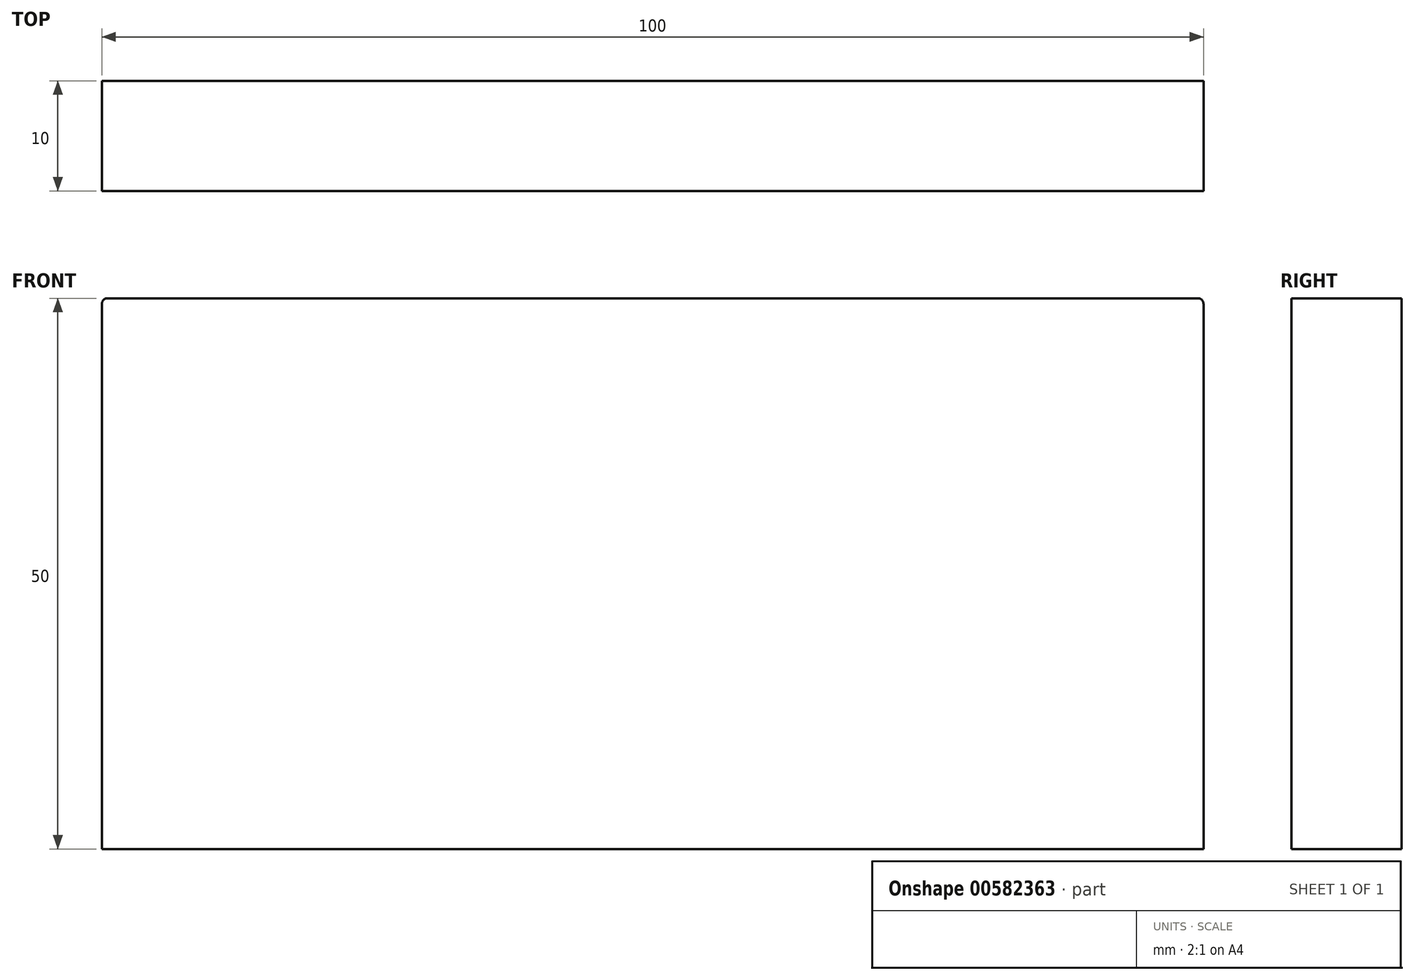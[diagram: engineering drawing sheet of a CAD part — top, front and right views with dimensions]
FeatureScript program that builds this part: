
annotation { "Feature Type Name" : "Feature", "Feature Type Description" : "" }
export const myFeature = defineFeature(function(context is Context, id is Id, definition is map)
    precondition{}
    {
        {
            var Q0;
            Q0=qCreatedBy(makeId("Front.planeOp"),FACE);
            var sketch = newSketch(context, id + "F0", { "sketchPlane" : qUnion([Q0])});
            skLineSegment(sketch, "E0.bottom", {"start": v(49.5, 25) * mm, "end": v(-49.5, 25) * mm});
            skLineSegment(sketch, "E0.top", {"start": v(50, -25) * mm, "end": v(-50, -25) * mm});
            skLineSegment(sketch, "E0.left", {"start": v(50, 24.5) * mm, "end": v(50, -25) * mm});
            skLineSegment(sketch, "E0.right", {"start": v(-50, 24.5) * mm, "end": v(-50, -25) * mm});
            skPoint(sketch, "E0.middle", {"position": v(0, 0) * mm});
            skPoint(sketch, "E1.visualSharp", {"position": v(50, 25) * mm});
            skArc(sketch, "E1.filletArc", {"start": v(50, 24.5) * mm, "mid": v(49.85, 24.85) * mm, "end": v(49.5, 25) * mm});
            skPoint(sketch, "E2.visualSharp", {"position": v(-50, 25) * mm});
            skArc(sketch, "E2.filletArc", {"start": v(-49.5, 25) * mm, "mid": v(-49.85, 24.85) * mm, "end": v(-50, 24.5) * mm});
            skSolve(sketch);
        }
        {
            var Q0;
            Q0=makeQuery(id+"F0.imprint","IMPRINT",FACE,{"disambiguationData":[TD([[makeQuery(id+"F0.imprint","IMPRINT",EDGE,{"derivedFrom":sQuery(id+"F0.wireOp",EDGE,"E0.bottom")}),1.0]])]});
            extrude(context, id + "F1", {"entities" : qUnion([Q0]), "depth" : 10 * mm, "offsetDistance" : 25 * mm});
        }
    });
